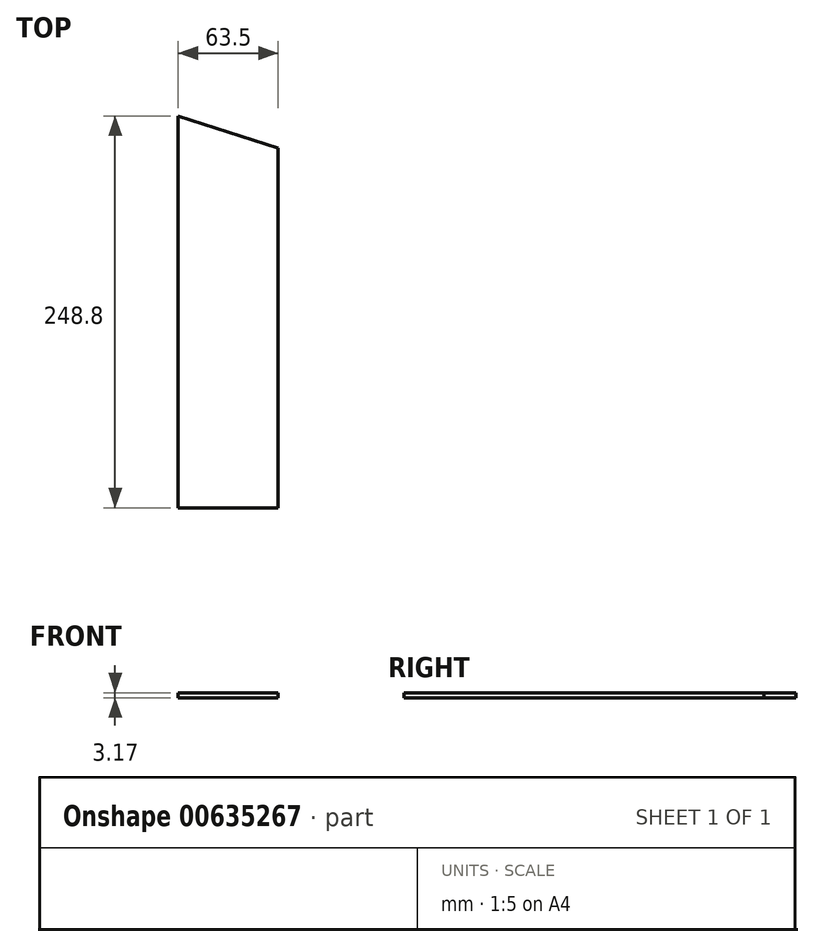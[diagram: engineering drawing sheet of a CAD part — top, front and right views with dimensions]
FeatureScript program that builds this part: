
annotation { "Feature Type Name" : "Feature", "Feature Type Description" : "" }
export const myFeature = defineFeature(function(context is Context, id is Id, definition is map)
    precondition{}
    {
        {
            var Q0;
            Q0=qCreatedBy(makeId("Top.planeOp"),FACE);
            var sketch = newSketch(context, id + "F0", { "sketchPlane" : qUnion([Q0])});
            skLineSegment(sketch, "E0.bottom", {"start": v(31.75, 114.3) * mm, "end": v(-31.75, 114.3) * mm});
            skLineSegment(sketch, "E0.top", {"start": v(31.75, -114.3) * mm, "end": v(-31.75, -114.3) * mm});
            skLineSegment(sketch, "E0.left", {"start": v(31.75, 114.3) * mm, "end": v(31.75, -114.3) * mm});
            skLineSegment(sketch, "E0.right", {"start": v(-31.75, 114.3) * mm, "end": v(-31.75, -114.3) * mm});
            skPoint(sketch, "E0.middle", {"position": v(0, 0) * mm});
            skLineSegment(sketch, "E1", {"start": v(-31.75, 114.3) * mm, "end": v(-31.75, 134.5) * mm});
            skLineSegment(sketch, "E2", {"start": v(-31.75, 134.5) * mm, "end": v(31.75, 114.3) * mm});
            skSolve(sketch);
        }
        {
            var Q0;
            Q0 = qSketchRegion(id + "F0", true);
            extrude(context, id + "F1", {"entities" : qUnion([Q0]), "depth" : 3.17 * mm, "offsetDistance" : 25.4 * mm});
        }
    });
